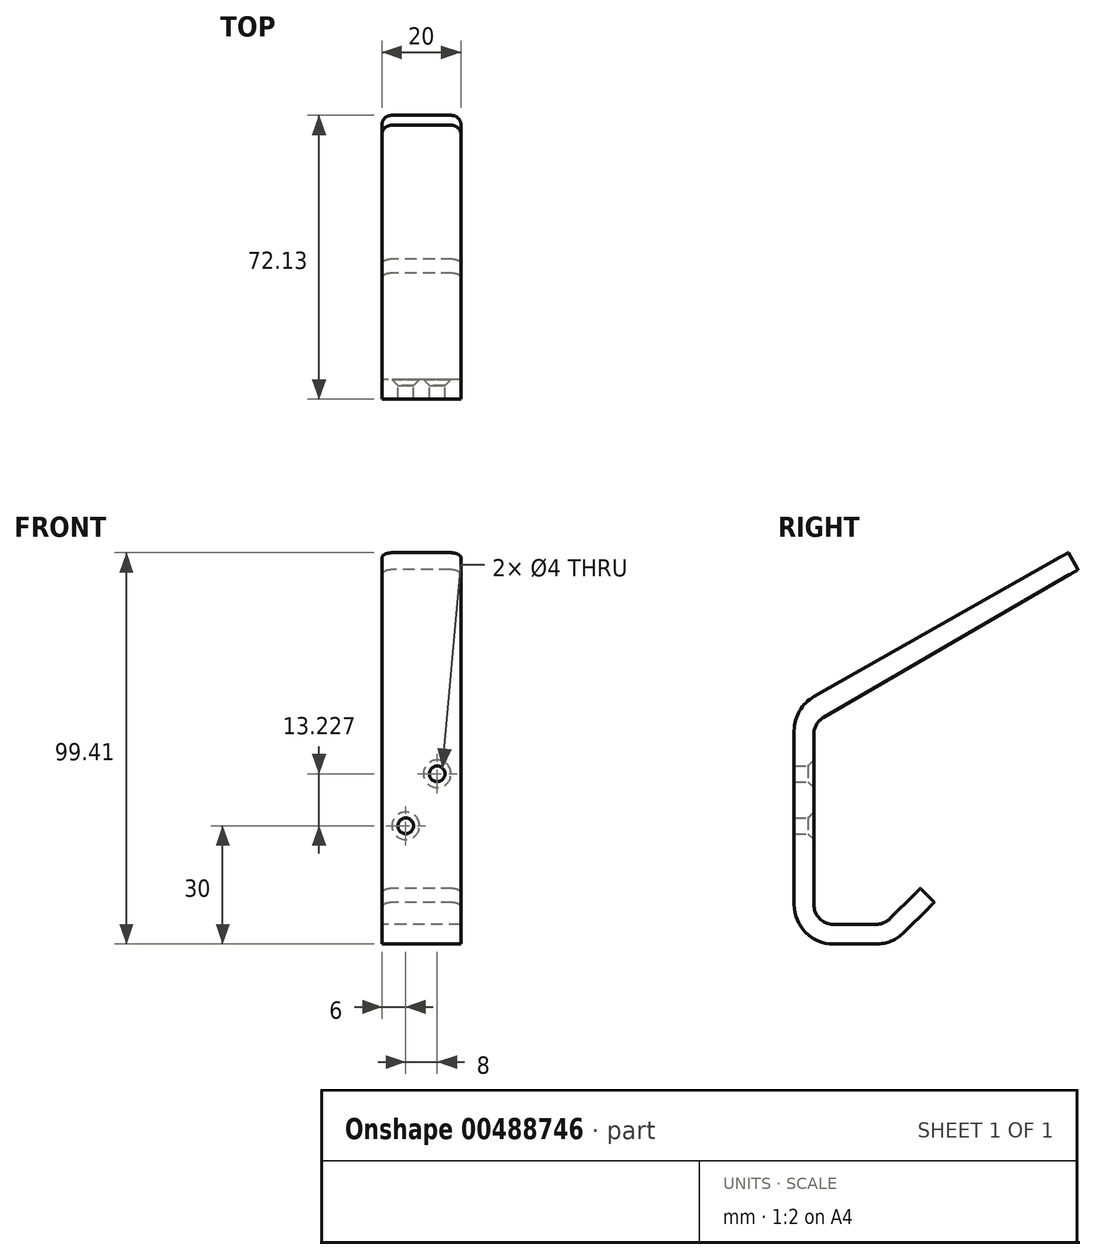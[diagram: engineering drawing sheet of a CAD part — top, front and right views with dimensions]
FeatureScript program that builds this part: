
annotation { "Feature Type Name" : "Feature", "Feature Type Description" : "" }
export const myFeature = defineFeature(function(context is Context, id is Id, definition is map)
    precondition{}
    {
        {
            var Q0;
            Q0=qCreatedBy(makeId("Right.planeOp"),FACE);
            var sketch = newSketch(context, id + "F0", { "sketchPlane" : qUnion([Q0])});
            skLineSegment(sketch, "E0", {"start": v(0, 0) * mm, "end": v(0, 60) * mm});
            skLineSegment(sketch, "E1", {"start": v(0, 60) * mm, "end": v(69.62, 99.4) * mm});
            skLineSegment(sketch, "E2", {"start": v(0, 0) * mm, "end": v(25, 0) * mm});
            skLineSegment(sketch, "E3", {"start": v(35.6, 10.6) * mm, "end": v(25, 0) * mm});
            skLineSegment(sketch, "E4", {"start": v(5, 5) * mm, "end": v(22.93, 5) * mm});
            skLineSegment(sketch, "E5", {"start": v(5, 5) * mm, "end": v(5, 56.1) * mm});
            skLineSegment(sketch, "E6", {"start": v(5, 56.1) * mm, "end": v(72.13, 95.08) * mm});
            skLineSegment(sketch, "E7", {"start": v(69.62, 99.4) * mm, "end": v(72.13, 95.08) * mm});
            skPoint(sketch, "E8.end.orphan", {"position": v(25, 15.81) * mm});
            skLineSegment(sketch, "E9", {"start": v(35.6, 10.6) * mm, "end": v(32.07, 14.14) * mm});
            skLineSegment(sketch, "E10", {"start": v(32.07, 14.14) * mm, "end": v(22.93, 5) * mm});
            skSolve(sketch);
        }
        {
            var Q0;
            Q0=makeQuery(id+"F0.imprint","IMPRINT",FACE,{"disambiguationData":[TD([[makeQuery(id+"F0.imprint","IMPRINT",EDGE,{"derivedFrom":sQuery(id+"F0.wireOp",EDGE,"E0")}),-1.0]])]});
            var Q1;
            Q1=sQuery(id+"F0.wireOp",EDGE,"E1");
            var Q2;
            Q2=sQuery(id+"F0.wireOp",EDGE,"E6");
            var Q3;
            Q3=sQuery(id+"F0.wireOp",EDGE,"E5");
            var Q4;
            Q4=sQuery(id+"F0.wireOp",EDGE,"E0");
            var Q5;
            Q5=sQuery(id+"F0.wireOp",EDGE,"cOYLGdv4-W0kR-WeMO-GZSo-5uf1Yx7Vsqno");
            var Q6;
            Q6=sQuery(id+"F0.wireOp",EDGE,"E8");
            var Q7;
            Q7=sQuery(id+"F0.wireOp",EDGE,"E3");
            var Q8;
            Q8=sQuery(id+"F0.wireOp",EDGE,"E4");
            var Q9;
            Q9=sQuery(id+"F0.wireOp",EDGE,"E2");
            var Q10;
            Q10=sQuery(id+"F0.wireOp",EDGE,"s3ZiQkoa-80Td-NgJe-TmCq-t2gHYK6hVpht");
            extrude(context, id + "F1", {"entities" : qUnion([Q0]), "surfaceEntities" : qUnion([Q1, Q2, Q3, Q4, Q5, Q6, Q7, Q8, Q9, Q10]), "depth" : 20 * mm, "offsetDistance" : 25 * mm});
        }
        {
            var Q0;
            Q0=makeQuery(id+"F1.opExtrude","SWEPT_EDGE",EDGE,{"disambiguationData":[OSD([sQuery(id+"F0.wireOp",EDGE,"E0"),sQuery(id+"F0.wireOp",EDGE,"E1")])]});
            var Q1;
            Q1=makeQuery(id+"F1.opExtrude","SWEPT_EDGE",EDGE,{"disambiguationData":[OSD([sQuery(id+"F0.wireOp",EDGE,"E0"),sQuery(id+"F0.wireOp",EDGE,"E2")])]});
            var Q2;
            Q2=makeQuery(id+"F1.opExtrude","SWEPT_EDGE",EDGE,{"disambiguationData":[OSD([sQuery(id+"F0.wireOp",EDGE,"E2"),sQuery(id+"F0.wireOp",EDGE,"E3")])]});
            fillet(context, id + "F2", {"entities" : qUnion([Q0, Q1, Q2]), "radius" : 10 * mm, "tangentPropagation" : true, "allowEdgeOverflow" : false});
        }
        {
            var Q0;
            Q0=makeQuery(id+"F1.opExtrude","SWEPT_EDGE",EDGE,{"disambiguationData":[OSD([sQuery(id+"F0.wireOp",EDGE,"E5"),sQuery(id+"F0.wireOp",EDGE,"E6")])]});
            var Q1;
            Q1=makeQuery(id+"F1.opExtrude","SWEPT_EDGE",EDGE,{"disambiguationData":[OSD([sQuery(id+"F0.wireOp",EDGE,"E4"),sQuery(id+"F0.wireOp",EDGE,"E5")])]});
            fillet(context, id + "F3", {"entities" : qUnion([Q0, Q1]), "radius" : 5 * mm, "tangentPropagation" : true, "allowEdgeOverflow" : false});
        }
        {
            var Q0;
            Q0=makeQuery(id+"F1.opExtrude","SWEPT_EDGE",EDGE,{"disambiguationData":[OSD([sQuery(id+"F0.wireOp",EDGE,"E4"),sQuery(id+"F0.wireOp",EDGE,"E10")])]});
            fillet(context, id + "F4", {"entities" : qUnion([Q0]), "radius" : 5 * mm, "tangentPropagation" : true, "allowEdgeOverflow" : false});
        }
        {
            var Q0;
            Q0=makeQuery(id+"F1.opExtrude","CAP_EDGE",EDGE,{"disambiguationData":[OSD([sQuery(id+"F0.wireOp",EDGE,"E9")])],"isStart":false});
            var Q1;
            Q1=makeQuery(id+"F1.opExtrude","CAP_EDGE",EDGE,{"disambiguationData":[OSD([sQuery(id+"F0.wireOp",EDGE,"E9")])],"isStart":true});
            fillet(context, id + "F5", {"entities" : qUnion([Q0, Q1]), "radius" : 2 * mm, "tangentPropagation" : true, "allowEdgeOverflow" : false});
        }
        {
            var Q0;
            Q0=makeQuery(id+"F1.opExtrude","CAP_EDGE",EDGE,{"disambiguationData":[OSD([sQuery(id+"F0.wireOp",EDGE,"E7")])],"isStart":false});
            var Q1;
            Q1=makeQuery(id+"F1.opExtrude","CAP_EDGE",EDGE,{"disambiguationData":[OSD([sQuery(id+"F0.wireOp",EDGE,"E7")])],"isStart":true});
            fillet(context, id + "F6", {"entities" : qUnion([Q0, Q1]), "radius" : 2.5 * mm, "tangentPropagation" : true, "allowEdgeOverflow" : false});
        }
        {
            var Q0;
            Q0=makeQuery(id+"F1.opExtrude","SWEPT_FACE",FACE,{"disambiguationData":[OSD([sQuery(id+"F0.wireOp",EDGE,"E5")])]});
            var sketch = newSketch(context, id + "F7", { "sketchPlane" : qUnion([Q0])});
            skPoint(sketch, "E11", {"position": v(-14, 43.23) * mm});
            skPoint(sketch, "E12", {"position": v(-6, 30) * mm});
            skSolve(sketch);
        }
        {
            var Q0;
            Q0=sQuery(id+"F7.wireOp",VERTEX,"E12");
            var Q1;
            Q1=sQuery(id+"F7.wireOp",VERTEX,"E11");
            var Q2;
            Q2=makeQuery(id+"F1.opExtrude","SWEPT_BODY",BODY,{"disambiguationData":[OSD([sQuery(id+"F0.wireOp",EDGE,"E0"),sQuery(id+"F0.wireOp",EDGE,"E1"),sQuery(id+"F0.wireOp",EDGE,"E2"),sQuery(id+"F0.wireOp",EDGE,"E3"),sQuery(id+"F0.wireOp",EDGE,"E4"),sQuery(id+"F0.wireOp",EDGE,"E5"),sQuery(id+"F0.wireOp",EDGE,"E6"),sQuery(id+"F0.wireOp",EDGE,"E7"),sQuery(id+"F0.wireOp",EDGE,"E9"),sQuery(id+"F0.wireOp",EDGE,"E10")])]});
            hole(context, id + "F8", {"style" : HoleStyle.C_SINK, "endStyle" : HoleEndStyle.THROUGH, "holeDiameter" : 4 * mm, "cSinkDiameter" : 7 * mm, "cSinkAngle" : 90 * degree, "isTappedThrough" : true, "tappedDepth" : 12 * mm, "tapClearance" : 3, "locations" : qUnion([Q0, Q1]), "scope" : qUnion([Q2])});
        }
    });
